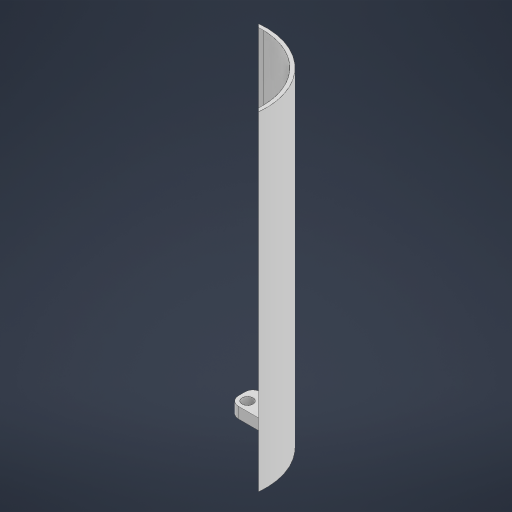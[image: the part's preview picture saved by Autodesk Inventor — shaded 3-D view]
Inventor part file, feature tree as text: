
AUTODESK INVENTOR PART (.ipt)
format: ipt  version: 2024 (Build 280153000, 153)  size: 203,776 bytes
history: native  units: mm
features: extrude x2, sketch x2, other x1, fillet x1, projected_geometry x1
ambient origin geometry x8: Origin, YZ Plane, XZ Plane, XY Plane, X Axis, Y Axis, Z Axis, Center Point
bodies: Body1 (feature_tree)
feature tree (7):
  other  "솔리드1"
  extrude  "돌출1"  Depth=25.0mm
  extrude  "돌출2"  TaperAngle=45.0deg  [1 undecoded]
  fillet  "모깎기1"  Radius=18.0mm
  sketch  "스케치1"
  sketch  "스케치2"
  projected_geometry  "투영된 루프1"
note: 1 required parameter value undecoded (feature->parameter linkage not recoverable at this tier; creation-order binding heuristic only, values carry confidence <= 0.55)
